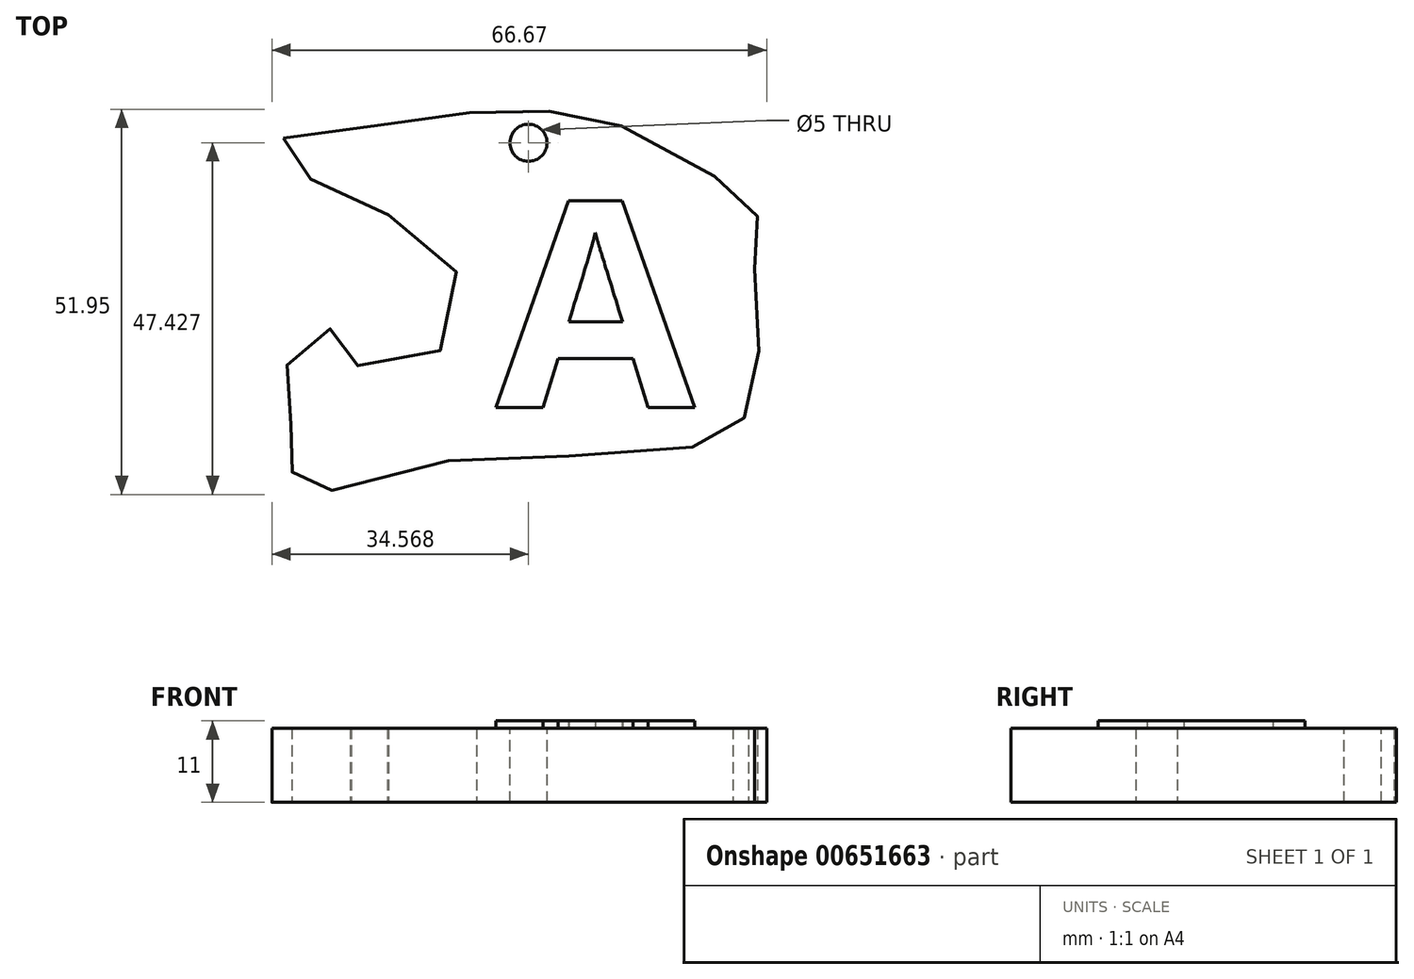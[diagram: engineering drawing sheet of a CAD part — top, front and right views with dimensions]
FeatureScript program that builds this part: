
annotation { "Feature Type Name" : "Feature", "Feature Type Description" : "" }
export const myFeature = defineFeature(function(context is Context, id is Id, definition is map)
    precondition{}
    {
        {
            var Q0;
            Q0=qCreatedBy(makeId("Top.planeOp"),FACE);
            var sketch = newSketch(context, id + "F0", { "sketchPlane" : qUnion([Q0])});
            skFitSpline(sketch, "E0", {"points": [v(-64.72, 51.56) * mm, v(-54.9, 52.88) * mm, v(-42.78, 54.51) * mm, v(-36.2, 55.19) * mm, v(-28.26, 55.19) * mm, v(-23.76, 55.19) * mm, v(-11.8, 49.01) * mm, v(-3.87, 44.91) * mm, v(-1.02, 42.22) * mm, v(-1.2, 39.32) * mm, v(-2.02, 36.02) * mm, v(0, 31.07) * mm, v(-1.11, 21.79) * mm, v(-4.03, 15.28) * mm, v(-1.22, 12.37) * mm, v(-11.97, 9.61) * mm, v(-29.23, 8.6) * mm, v(-46.9, 7.3) * mm, v(-60.29, 3.54) * mm, v(-62.02, 3.94) * mm, v(-63.42, 6.42) * mm, v(-66.23, 8.34) * mm, v(-63.6, 13.66) * mm, v(-66.23, 19.28) * mm, v(-61.63, 22.5) * mm, v(-61, 24.7) * mm, v(-56.02, 25.51) * mm, v(-55.66, 22.05) * mm, v(-53.48, 20.45) * mm, v(-44.19, 22.54) * mm, v(-39.04, 31.06) * mm, v(-50.45, 39.24) * mm, v(-50.69, 42.01) * mm, v(-60.68, 45.8) * mm, v(-66.23, 50.98) * mm, v(-64.72, 51.56) * mm]});
            skSolve(sketch);
        }
        {
            var Q0;
            Q0 = qSketchRegion(id + "F0", true);
            extrude(context, id + "F1", {"entities" : qUnion([Q0]), "depth" : 10 * mm, "offsetDistance" : 25 * mm});
        }
        {
            var Q0;
            Q0=makeQuery(id+"F1.opExtrude","CAP_FACE",FACE,{"disambiguationData":[OSD([sQuery(id+"F0.wireOp",EDGE,"E0")])],"isStart":false});
            var sketch = newSketch(context, id + "F2", { "sketchPlane" : qUnion([Q0])});
            skText(sketch, "E1", { "text": "A", "fontName": "OpenSans-Bold.ttf"});
            const initialGuessF2  = {"E1": [-0.03608, 0.01523, 1, 0, 0.02799]};
            skSetInitialGuess(sketch, initialGuessF2);
            skSolve(sketch);
        }
        {
            var Q0;
            Q0 = qSketchRegion(id + "F2", true);
            extrude(context, id + "F3", {"entities" : qUnion([Q0]), "operationType" : NewBodyOperationType.ADD, "depth" : 1 * mm, "offsetDistance" : 25 * mm});
        }
        {
            var Q0;
            {var subQ0=sQuery(id+"F0.wireOp",EDGE,"E0");Q0=makeQuery(id+"F3.boolean.opBoolean","SPLIT",FACE,{"disambiguationData":[TD([makeQuery(id+"F1.opExtrude","SWEPT_FACE",FACE,{"disambiguationData":[OSD([subQ0])]})])],"derivedFrom":makeQuery(id+"F1.opExtrude","CAP_FACE",FACE,{"disambiguationData":[OSD([subQ0])],"isStart":false})});}
            var sketch = newSketch(context, id + "F4", { "sketchPlane" : qUnion([Q0])});
            skCircle(sketch, "E2", {"center": v(-31.7, 50.9) * mm, "radius": 2.92 * mm});
            skSolve(sketch);
        }
        {
            var Q0;
            Q0=sQuery(id+"F4.wireOp",VERTEX,"E2.center");
            var Q1;
            Q1=makeQuery(id+"F1.opExtrude","SWEPT_BODY",BODY,{"disambiguationData":[OSD([sQuery(id+"F0.wireOp",EDGE,"E0")])]});
            hole(context, id + "F5", {"style" : HoleStyle.SIMPLE, "endStyle" : HoleEndStyle.THROUGH, "holeDiameter" : 5 * mm, "majorDiameter" : 5 * mm, "isTappedThrough" : true, "tappedDepth" : 12 * mm, "tapClearance" : 3, "locations" : qUnion([Q0]), "scope" : qUnion([Q1])});
        }
    });
